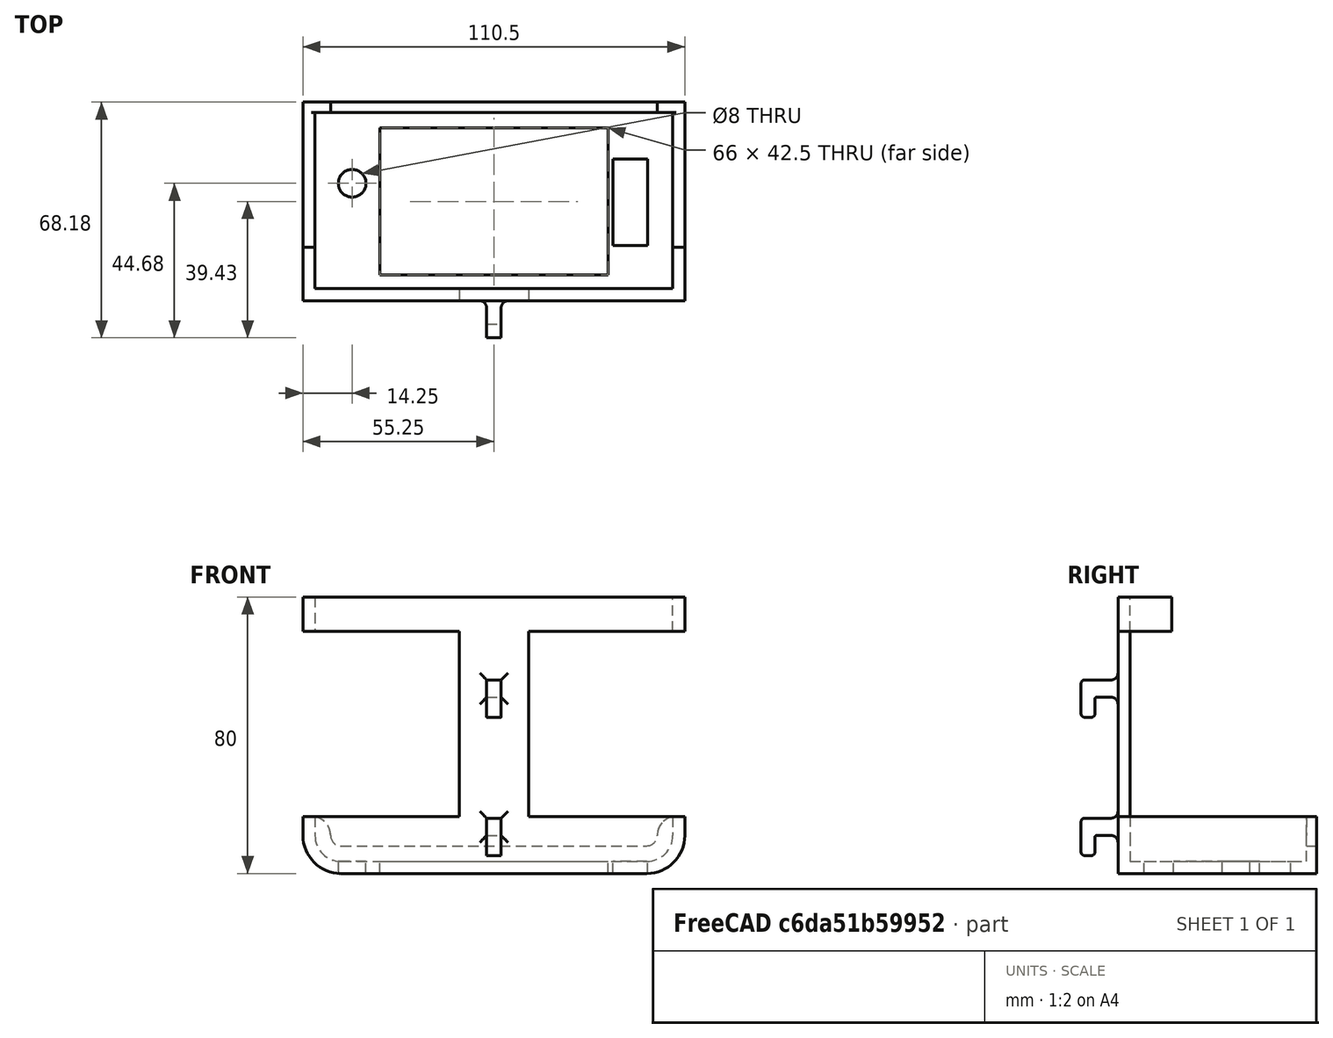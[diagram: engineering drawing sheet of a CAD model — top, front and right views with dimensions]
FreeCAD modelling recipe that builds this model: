
FCSTD DOCUMENT  (FreeCAD 1.1R20260414 (Git shallow))
Label: Urban_skadis_wall_mount
License: All rights reserved
LicenseURL: https://en.wikipedia.org/wiki/All_rights_reserved
objects: Sketcher::SketchObject×6, PartDesign::Pad×5, PartDesign::Pocket×1, App::Point×1, PartDesign::Plane×1, PartDesign::LinearPattern×1, Spreadsheet::Sheet×1, Mesh::Feature×1, PartDesign::Fillet×1, PartDesign::Body×1
note: 37 computed .brp shape members not serialized (recipe doc carries the construction recipe); baked Part::Feature solids carry a one-line shape summary decoded from their .brp

FEATURE [Sketcher::SketchObject] Sketch067
  ArcFitTolerance = 1e-06
  AttachmentSupport = -> [XZ_Plane012]
  ExternalTypes = [0]
  FullyConstrained = true
  MakeInternals = false
  MapMode = 5
  Placement = pos=(0,0,0) rot=(1,0,0;1.5708rad)
  _ExternalGeoVersion = 0
  sketch-geometry (14):
    g0: LineSegment StartX=55.25 StartY=24 StartZ=0 EndX=-55.25 EndY=24 EndZ=0
    g1: LineSegment StartX=-55.25 StartY=24 StartZ=0 EndX=-55.25 EndY=14 EndZ=0
    g2: LineSegment StartX=-55.25 StartY=14 StartZ=0 EndX=-10 EndY=14 EndZ=0
    g3: LineSegment StartX=-10 StartY=14 StartZ=0 EndX=-10 EndY=-39.5 EndZ=0
    g4: LineSegment StartX=-10 StartY=-39.5 StartZ=0 EndX=-55.25 EndY=-39.5 EndZ=0
    g5: LineSegment StartX=-55.25 StartY=-39.5 StartZ=0 EndX=-55.25 EndY=-45 EndZ=0
    g6: LineSegment StartX=55.25 StartY=24 StartZ=0 EndX=55.25 EndY=14 EndZ=0
    g7: LineSegment StartX=55.25 StartY=14 StartZ=0 EndX=10 EndY=14 EndZ=0
    g8: LineSegment StartX=10 StartY=14 StartZ=0 EndX=10 EndY=-39.5 EndZ=0
    g9: LineSegment StartX=10 StartY=-39.5 StartZ=0 EndX=55.25 EndY=-39.5 EndZ=0
    g10: LineSegment StartX=55.25 StartY=-39.5 StartZ=0 EndX=55.25 EndY=-45 EndZ=0
    g11: ArcOfCircle CenterX=44.25 CenterY=-45 CenterZ=0 NormalX=0 NormalY=0 NormalZ=1 AngleXU=0 Radius=11 StartAngle=4.71239 EndAngle=6.28319
    g12: ArcOfCircle CenterX=-44.25 CenterY=-45 CenterZ=0 NormalX=0 NormalY=0 NormalZ=1 AngleXU=0 Radius=11 StartAngle=3.14159 EndAngle=4.71239
    g13: LineSegment StartX=44.25 StartY=-56 StartZ=0 EndX=-44.25 EndY=-56 EndZ=0
  constraints (42):
    c: Horizontal(g0)
    c: Coincident(g0,g1)
    c: Vertical(g1)
    c: Coincident(g1,g2)
    c: Horizontal(g2)
    c: Coincident(g2,g3)
    c: Vertical(g3)
    c: Coincident(g3,g4)
    c: Horizontal(g4)
    c: Coincident(g4,g5)
    c: Vertical(g5)
    c: Coincident(g0,g6)
    c: Vertical(g6)
    c: Coincident(g6,g7)
    c: Horizontal(g7)
    c: Coincident(g7,g8)
    c: Vertical(g8)
    c: Coincident(g8,g9)
    c: Horizontal(g9)
    c: Coincident(g9,g10)
    c: Vertical(g10)
    c: Coincident(g11,g10)
    c: Coincident(g12,g5)
    c: Coincident(g13,g11)
    c: Coincident(g13,g12)
    c: Horizontal(g13)
    c: Symmetric(g7,g2,g-2)
    c: Distance(g3,g8) = 20
    c: Distance(g13,g0) = 80
    c: Horizontal(g10,g11)
    c: Horizontal(g12,g5)
    c: Vertical(g12,g12)
    c: Vertical(g11,g11)
    c: Equal(g12,g11)
    c: Distance(g-1,g13) = 56
    c: Symmetric(g9,g4,g-2)
    c: Distance(g13,g4) = 16.5
    c: DistanceY(g1,g1) = 10
    c: Vertical(g1,g4)
    c: Vertical(g6,g9)
    c: DistanceX(g0,g0) = 110.5
    c: Radius(g12) = 11
FEATURE [PartDesign::Pad] Pad050
  Direction = (0,-1,2e-16)
  Length = 3.5
  Length2 = 10
  Placement = pos=(0,0,0) rot=(1,0,0;1.5708rad)
  Profile = -> Sketch067
  ReferenceAxis = -> Sketch067 [N_Axis]
  Refine = true
  SideType = 0
  Suppressed = false
  Type = 0
  Type2 = 0
FEATURE [Sketcher::SketchObject] Sketch068
  ArcFitTolerance = 1e-06
  AttachmentSupport = -> [Pad050]
  ExternalTypes = [0]
  FullyConstrained = true
  MakeInternals = false
  MapMode = 5
  Placement = pos=(0,-3.1e-15,0) rot=(-1,0,0;1.5708rad)
  _ExternalGeoVersion = 0
  sketch-geometry (12):
    g0: LineSegment StartX=-55.25 StartY=45 StartZ=0 EndX=-55.25 EndY=39.5 EndZ=0
    g1: LineSegment StartX=-44.25 StartY=56 StartZ=0 EndX=44.25 EndY=56 EndZ=0
    g2: LineSegment StartX=-44.25 StartY=52.5 StartZ=0 EndX=44.25 EndY=52.5 EndZ=0
    g3: LineSegment StartX=-55.25 StartY=39.5 StartZ=0 EndX=-51.75 EndY=39.5 EndZ=0
    g4: LineSegment StartX=55.25 StartY=45 StartZ=0 EndX=55.25 EndY=39.5 EndZ=0
    g5: LineSegment StartX=55.25 StartY=39.5 StartZ=0 EndX=51.75 EndY=39.5 EndZ=0
    g6: LineSegment StartX=51.75 StartY=39.5 StartZ=0 EndX=51.75 EndY=45 EndZ=0
    g7: LineSegment StartX=-51.75 StartY=39.5 StartZ=0 EndX=-51.75 EndY=45 EndZ=0
    g8: ArcOfCircle CenterX=-44.25 CenterY=45 CenterZ=0 NormalX=0 NormalY=0 NormalZ=1 AngleXU=0 Radius=7.5 StartAngle=1.5708 EndAngle=3.14159
    g9: ArcOfCircle CenterX=44.25 CenterY=45 CenterZ=0 NormalX=0 NormalY=0 NormalZ=1 AngleXU=0 Radius=7.5 StartAngle=0 EndAngle=1.5708
    g10: ArcOfCircle CenterX=44.25 CenterY=45 CenterZ=0 NormalX=0 NormalY=0 NormalZ=1 AngleXU=0 Radius=11 StartAngle=0 EndAngle=1.5708
    g11: ArcOfCircle CenterX=-44.25 CenterY=45 CenterZ=0 NormalX=0 NormalY=0 NormalZ=1 AngleXU=0 Radius=11 StartAngle=1.5708 EndAngle=3.14159
  constraints (37):
    c: Vertical(g0)
    c: Horizontal(g1)
    c: Coincident(g3,g0)
    c: Horizontal(g3)
    c: Vertical(g4)
    c: Coincident(g5,g4)
    c: Horizontal(g5)
    c: Coincident(g6,g5)
    c: Vertical(g6)
    c: Coincident(g7,g3)
    c: Vertical(g7)
    c: Coincident(g8,g7)
    c: Coincident(g8,g2)
    c: Coincident(g9,g2)
    c: Coincident(g9,g6)
    c: Coincident(g10,g9)
    c: Coincident(g10,g1)
    c: Coincident(g10,g4)
    c: Coincident(g11,g8)
    c: Coincident(g11,g0)
    c: Coincident(g11,g1)
    c: Vertical(g10,g2)
    c: Vertical(g1,g9)
    c: Horizontal(g6,g9)
    c: Horizontal(g4,g9)
    c: Horizontal(g7,g8)
    c: Horizontal(g0,g8)
    c: Vertical(g8,g2)
    c: Vertical(g1,g8)
    c: Radius(g11) = 11
    c: Radius(g8) = 7.5
    c: Distance(g1,g-1) = 56
    c: Equal(g8,g9)
    c: Horizontal(g5,g3)
    c: DistanceY(g4,g4) = 5.5
    c: Distance(g6,g7) = 103.5
    c: Symmetric(g2,g2,g-2)
FEATURE [PartDesign::Pad] Pad051
  BaseFeature = -> Pad050
  Direction = (0,1,2e-16)
  Length = 51
  Length2 = 10
  Placement = pos=(0,0,0) rot=(1,0,0;1.5708rad)
  Profile = -> Sketch068
  ReferenceAxis = -> Sketch068 [N_Axis]
  Refine = true
  SideType = 0
  Suppressed = false
  Type = 0
  Type2 = 0
FEATURE [Sketcher::SketchObject] Sketch071
  ArcFitTolerance = 1e-06
  AttachmentSupport = -> [Pad051]
  ExternalTypes = [0]
  FullyConstrained = true
  MakeInternals = false
  MapMode = 5
  Placement = pos=(0,-3.1e-15,0) rot=(-1,0,0;1.5708rad)
  _ExternalGeoVersion = 0
  sketch-geometry (8):
    g0: LineSegment StartX=-55.25 StartY=-14 StartZ=0 EndX=-55.25 EndY=-24 EndZ=0
    g1: LineSegment StartX=-55.25 StartY=-24 StartZ=0 EndX=-51.75 EndY=-24 EndZ=0
    g2: LineSegment StartX=-51.75 StartY=-24 StartZ=0 EndX=-51.75 EndY=-14 EndZ=0
    g3: LineSegment StartX=-51.75 StartY=-14 StartZ=0 EndX=-55.25 EndY=-14 EndZ=0
    g4: LineSegment StartX=51.75 StartY=-14 StartZ=0 EndX=51.75 EndY=-24 EndZ=0
    g5: LineSegment StartX=51.75 StartY=-24 StartZ=0 EndX=55.25 EndY=-24 EndZ=0
    g6: LineSegment StartX=55.25 StartY=-24 StartZ=0 EndX=55.25 EndY=-14 EndZ=0
    g7: LineSegment StartX=55.25 StartY=-14 StartZ=0 EndX=51.75 EndY=-14 EndZ=0
  constraints (23):
    c: Coincident(g0,g1)
    c: Coincident(g1,g2)
    c: Coincident(g2,g3)
    c: Coincident(g3,g0)
    c: Vertical(g0)
    c: Vertical(g2)
    c: Horizontal(g1)
    c: Horizontal(g3)
    c: Distance(g0,g2) = 3.5
    c: Distance(g1,g3) = 10
    c: Coincident(g4,g5)
    c: Coincident(g5,g6)
    c: Coincident(g6,g7)
    c: Coincident(g7,g4)
    c: Vertical(g4)
    c: Vertical(g6)
    c: Horizontal(g5)
    c: Horizontal(g7)
    c: Equal(g4,g0)
    c: Equal(g3,g7)
    c: Symmetric(g2,g4,g-2)
    c: Distance(g4,g2) = 103.5
    c: Distance(g-1,g7) = 14
FEATURE [Sketcher::SketchObject] Sketch069
  ArcFitTolerance = 1e-06
  AttachmentSupport = -> [Pad051]
  ExternalTypes = [0]
  FullyConstrained = true
  MakeInternals = false
  MapMode = 5
  Placement = pos=(0,51,0) rot=(-1,0,0;1.5708rad)
  _ExternalGeoVersion = 0
  sketch-geometry (12):
    g0: LineSegment StartX=-55.25 StartY=45 StartZ=0 EndX=-55.25 EndY=39.5 EndZ=0
    g1: LineSegment StartX=-44.25 StartY=56 StartZ=0 EndX=44.25 EndY=56 EndZ=0
    g2: LineSegment StartX=-44.25 StartY=48 StartZ=0 EndX=44.25 EndY=48 EndZ=0
    g3: LineSegment StartX=-55.25 StartY=39.5 StartZ=0 EndX=-52.75 EndY=39.5 EndZ=0
    g4: LineSegment StartX=55.25 StartY=45 StartZ=0 EndX=55.25 EndY=39.5 EndZ=0
    g5: LineSegment StartX=55.25 StartY=39.5 StartZ=0 EndX=52.75 EndY=39.5 EndZ=0
    g6: ArcOfCircle CenterX=-44.25 CenterY=45 CenterZ=0 NormalX=0 NormalY=0 NormalZ=1 AngleXU=0 Radius=3 StartAngle=1.5708 EndAngle=3.14159
    g7: ArcOfCircle CenterX=44.25 CenterY=45 CenterZ=0 NormalX=0 NormalY=0 NormalZ=1 AngleXU=0 Radius=3 StartAngle=0 EndAngle=1.5708
    g8: ArcOfCircle CenterX=44.25 CenterY=45 CenterZ=0 NormalX=0 NormalY=0 NormalZ=1 AngleXU=0 Radius=11 StartAngle=0 EndAngle=1.5708
    g9: ArcOfCircle CenterX=-44.25 CenterY=45 CenterZ=0 NormalX=0 NormalY=0 NormalZ=1 AngleXU=0 Radius=11 StartAngle=1.5708 EndAngle=3.14159
    g10: ArcOfCircle CenterX=52.75 CenterY=45 CenterZ=0 NormalX=0 NormalY=0 NormalZ=1 AngleXU=0 Radius=5.5 StartAngle=3.14159 EndAngle=4.71239
    g11: ArcOfCircle CenterX=-52.75 CenterY=45 CenterZ=0 NormalX=0 NormalY=0 NormalZ=1 AngleXU=0 Radius=5.5 StartAngle=4.71239 EndAngle=6.28319
  constraints (39):
    c: Vertical(g0)
    c: Horizontal(g2)
    c: Coincident(g3,g0)
    c: Horizontal(g3)
    c: Vertical(g4)
    c: Coincident(g5,g4)
    c: Horizontal(g5)
    c: Coincident(g6,g2)
    c: Coincident(g7,g2)
    c: Coincident(g8,g7)
    c: Coincident(g8,g1)
    c: Coincident(g8,g4)
    c: Coincident(g9,g6)
    c: Coincident(g9,g0)
    c: Coincident(g9,g1)
    c: Vertical(g8,g2)
    c: Vertical(g1,g7)
    c: Horizontal(g7,g7)
    c: Horizontal(g4,g7)
    c: Horizontal(g6,g6)
    c: Horizontal(g0,g6)
    c: Vertical(g6,g2)
    c: Vertical(g1,g6)
    c: Radius(g9) = 11
    c: Radius(g6) = 3
    c: Distance(g1,g-1) = 56
    c: Equal(g6,g7)
    c: Horizontal(g5,g3)
    c: DistanceY(g4,g4) = 5.5
    c: Coincident(g10,g7)
    c: Coincident(g10,g5)
    c: Coincident(g11,g6)
    c: Coincident(g11,g3)
    c: Horizontal(g11,g6)
    c: Vertical(g11,g3)
    c: Horizontal(g7,g10)
    c: Vertical(g5,g10)
    c: Symmetric(g1,g1,g-2)
    c: Distance(g4,g0) = 110.5
FEATURE [PartDesign::Pad] Pad052
  BaseFeature = -> Pad051
  Direction = (0,1,2e-16)
  Length = 3
  Length2 = 10
  Placement = pos=(0,0,0) rot=(1,0,0;1.5708rad)
  Profile = -> Sketch069
  ReferenceAxis = -> Sketch069 [N_Axis]
  Refine = true
  SideType = 0
  Suppressed = false
  Type = 0
  Type2 = 0
FEATURE [Sketcher::SketchObject] Sketch070
  ArcFitTolerance = 1e-06
  ExternalTypes = [0]
  FullyConstrained = true
  MakeInternals = false
  MapMode = 5
  Placement = pos=(0,-1.29e-14,-56) rot=(1,0,0;3.14159rad)
  _ExternalGeoVersion = 0
  sketch-geometry (9):
    g0: LineSegment StartX=-33 StartY=-4 StartZ=0 EndX=-33 EndY=-46.5 EndZ=0
    g1: LineSegment StartX=-33 StartY=-46.5 StartZ=0 EndX=33 EndY=-46.5 EndZ=0
    g2: LineSegment StartX=33 StartY=-46.5 StartZ=0 EndX=33 EndY=-4 EndZ=0
    g3: LineSegment StartX=33 StartY=-4 StartZ=0 EndX=-33 EndY=-4 EndZ=0
    g4: LineSegment StartX=34.5 StartY=-12.5 StartZ=0 EndX=34.5 EndY=-37.5 EndZ=0
    g5: LineSegment StartX=34.5 StartY=-37.5 StartZ=0 EndX=44.5 EndY=-37.5 EndZ=0
    g6: LineSegment StartX=44.5 StartY=-37.5 StartZ=0 EndX=44.5 EndY=-12.5 EndZ=0
    g7: LineSegment StartX=44.5 StartY=-12.5 StartZ=0 EndX=34.5 EndY=-12.5 EndZ=0
    g8: Circle CenterX=-41 CenterY=-30.5 CenterZ=0 NormalX=0 NormalY=0 NormalZ=1 AngleXU=0 Radius=4
  constraints (26):
    c: Coincident(g0,g1)
    c: Coincident(g1,g2)
    c: Coincident(g2,g3)
    c: Coincident(g3,g0)
    c: Vertical(g0)
    c: Vertical(g2)
    c: Horizontal(g3)
    c: Coincident(g4,g5)
    c: Coincident(g5,g6)
    c: Coincident(g6,g7)
    c: Coincident(g7,g4)
    c: Vertical(g4)
    c: Vertical(g6)
    c: Horizontal(g5)
    c: Horizontal(g7)
    c: DistanceY(g0,g0) = 42.5
    c: DistanceX(g3,g3) = 66
    c: Symmetric(g0,g1,g-2)
    c: DistanceY(g6,g6) = 25
    c: DistanceX(g7,g7) = 10
    c: Distance(g-1,g3) = 4
    c: Distance(g-1,g7) = 12.5
    c: DistanceY(g8,g-1) = 30.5
    c: Distance(g8,g-2) = 41
    c: Diameter(g8) = 8
    c: Distance(g-2,g4) = 34.5
FEATURE [PartDesign::Pocket] Pocket033
  BaseFeature = -> Pad052
  Direction = (0,1e-16,1)
  Length = 5
  Length2 = 5
  Placement = pos=(0,0,0) rot=(1,0,0;1.5708rad)
  Profile = -> Sketch070
  ReferenceAxis = -> Sketch070 [N_Axis]
  Refine = true
  SideType = 0
  Suppressed = false
  Type = 1
  Type2 = 0
FEATURE [PartDesign::Pad] Pad053
  BaseFeature = -> Pocket033
  Direction = (0,1,2e-16)
  Length = 12
  Length2 = 10
  Placement = pos=(0,0,0) rot=(1,0,0;1.5708rad)
  Profile = -> Sketch071
  ReferenceAxis = -> Sketch071 [N_Axis]
  Refine = true
  SideType = 0
  Suppressed = false
  Type = 0
  Type2 = 0
FEATURE [App::Point] Origin023  label="Origin"
  Role = Origin
FEATURE [PartDesign::Plane] DatumPlane
  AttachmentOffset = pos=(0,0,-10) rot=(0,0,1;0rad)
  AttachmentSupport = -> [Pad053]
  Length = 96.9988
  MapMode = 5
  Placement = pos=(0,0,2.2e-15) rot=(0.707107,0,0.707107;3.14159rad)
  ResizeMode = 0
  Width = 94.9988
FEATURE [Sketcher::SketchObject] Sketch
  ArcFitTolerance = 1e-06
  AttachmentSupport = -> [DatumPlane]
  ExternalTypes = [0]
  FullyConstrained = false
  MakeInternals = false
  MapMode = 5
  Placement = pos=(0,0,2.2e-15) rot=(0.707107,0,0.707107;3.14159rad)
  _ExternalGeoVersion = 1
  expr: Constraints[10] = <<Spreadsheet>>.HookGrab + 1
  expr: Constraints[11] = <<Spreadsheet>>.HookGrab
  expr: Constraints[32] = <<Spreadsheet>>.HookThiknessSide
  expr: Constraints[9] = <<Spreadsheet>>.HookThiknessSide + <<Spreadsheet>>.HookGrab
  sketch-geometry (14):
    g0: LineSegment StartX=0 StartY=3.38406 StartZ=0 EndX=0 EndY=13.1841 EndZ=0
    g1: LineSegment StartX=-1 StartY=14.1841 StartZ=0 EndX=-9.8 EndY=14.1841 EndZ=0
    g2: LineSegment StartX=-10.8 StartY=13.1841 StartZ=0 EndX=-10.8 EndY=11.1841 EndZ=0
    g3: LineSegment StartX=-9.8 StartY=10.1841 StartZ=0 EndX=-5.5 EndY=10.1841 EndZ=0
    g4: LineSegment StartX=-5 StartY=9.68406 StartZ=0 EndX=-5 EndY=3.38406 EndZ=0
    g5: LineSegment StartX=-5 StartY=3.38406 StartZ=0 EndX=0 EndY=3.38406 EndZ=0
    g6: ArcOfCircle CenterX=-9.8 CenterY=13.1841 CenterZ=0 NormalX=0 NormalY=0 NormalZ=1 AngleXU=0 Radius=1 StartAngle=1.5708 EndAngle=3.14159
    g7: GeomPoint [constr] X=-10.8 Y=14.1841 Z=0
    g8: ArcOfCircle CenterX=-9.8 CenterY=11.1841 CenterZ=0 NormalX=0 NormalY=0 NormalZ=1 AngleXU=0 Radius=1 StartAngle=3.14159 EndAngle=4.71239
    g9: GeomPoint [constr] X=-10.8 Y=10.1841 Z=0
    g10: ArcOfCircle CenterX=-5.5 CenterY=9.68406 CenterZ=0 NormalX=0 NormalY=0 NormalZ=1 AngleXU=0 Radius=0.5 StartAngle=-1.8e-15 EndAngle=1.5708
    g11: GeomPoint [constr] X=-5 Y=10.1841 Z=0
    g12: ArcOfCircle CenterX=-1 CenterY=13.1841 CenterZ=0 NormalX=0 NormalY=0 NormalZ=1 AngleXU=0 Radius=1 StartAngle=2e-16 EndAngle=1.5708
    g13: GeomPoint [constr] X=0 Y=14.1841 Z=0
  constraints (33):
    c: PointOnObject(g0,g-2)
    c: PointOnObject(g13,g-2)
    c: Horizontal(g1)
    c: Vertical(g2)
    c: Horizontal(g3)
    c: Vertical(g4)
    c: Coincident(g4,g5)
    c: Coincident(g5,g0)
    c: Horizontal(g5)
    c: DistanceY(g0,g13) = 10.8
    c: DistanceY(g4,g11) = 6.8
    c: DistanceX(g9,g11) = 5.8
    c: PointOnObject(g7,g1)
    c: PointOnObject(g7,g2)
    c: Tangent(g1,g6) = -1.5708
    c: Tangent(g2,g6) = -1.5708
    c: PointOnObject(g9,g2)
    c: PointOnObject(g9,g3)
    c: Tangent(g2,g8) = -1.5708
    c: Tangent(g3,g8) = -1.5708
    c: PointOnObject(g11,g3)
    c: PointOnObject(g11,g4)
    c: Tangent(g3,g10) = 1.5708
    c: Tangent(g4,g10) = 1.5708
    c: PointOnObject(g13,g0)
    c: PointOnObject(g13,g1)
    c: Tangent(g0,g12) = -1.5708
    c: Tangent(g1,g12) = -1.5708
    c: Radius(g6) = 1
    c: Radius(g12) = 1
    c: Radius(g10) = 0.5
    c: Radius(g8) = 1
    c: DistanceX(g5,g5) = 5
FEATURE [PartDesign::Pad] Pad  label="Hook Pad"
  BaseFeature = -> Pad053
  Direction = (1,0,-2e-16)
  Length = 4.2
  Length2 = 10
  Placement = pos=(0,0,0) rot=(1,0,0;1.5708rad)
  Profile = -> Sketch
  ReferenceAxis = -> Sketch [N_Axis]
  Refine = true
  SideType = 2
  Suppressed = false
  Type = 0
  Type2 = 0
  expr: Length = <<Spreadsheet>>.HookThikness
FEATURE [PartDesign::LinearPattern] LinearPattern
  BaseFeature = -> Pad
  Direction = -> Z_Axis012
  Direction2 = -> Z_Axis012
  Length = 40
  Length2 = 100
  Mode = 1
  Mode2 = 0
  Occurrences = 2
  Occurrences2 = 1
  Offset = 40
  Offset2 = 100
  Originals = -> [Pad]
  Placement = pos=(0,0,0) rot=(1,0,0;1.5708rad)
  Refine = true
  Reversed = true
  Reversed2 = false
  SpacingPattern = [40]
  SpacingPattern2 = [0]
  Spacings = [-1]
  Suppressed = false
  TransformMode = 0
FEATURE [Spreadsheet::Sheet] Spreadsheet
  cells = A1='SkadisOffset; B1(SkadisOffset)=0.8; A2='SkadisHoleWidth; B2(SkadisHoleWidth)=5; C2='Это и ширина отверстия и глубина; A3='SkadisHoleHeight; B3(SkadisHoleHeight)=15; A4='HookThikness; B4(HookThikness)==SkadisHoleWidth - SkadisOffset; C4='толщина крючка фас (когда вставляешь); A5='HookThiknessSide; B5(HookThiknessSide)==SkadisHoleHeight / 3; C5='толщина в профиль; A6='HookGrab; B6(HookGrab)==SkadisHoleWidth + SkadisOffset; C6='толщина захвата крюка
FEATURE [Mesh::Feature] skadis_board_16cm_16cm
  Placement = pos=(-128,-4,-127) rot=(1,0,0;1.5708rad)
FEATURE [PartDesign::Fillet] Fillet  label="Better Hook Mounts"
  Base = -> LinearPattern [Edge92,Edge90,Edge89,Edge91,Edge85,Edge88,Edge87,Edge86]
  BaseFeature = -> LinearPattern
  Placement = pos=(0,0,0) rot=(1,0,0;1.5708rad)
  Radius = 2
  Refine = true
  SupportTransform = false
  Suppressed = false
  UseAllEdges = false
FEATURE [PartDesign::Body] Body012  label="Wall_Mount"
  AllowCompound = false
  Group = -> [Sketch067,Pad050,Sketch068,Pad051,Sketch069,Pad052,Sketch070,Pocket033,Sketch071,Pad053,DatumPlane,Sketch,Pad,LinearPattern,Fillet]
  Origin = -> Origin012
  Tip = -> Fillet
